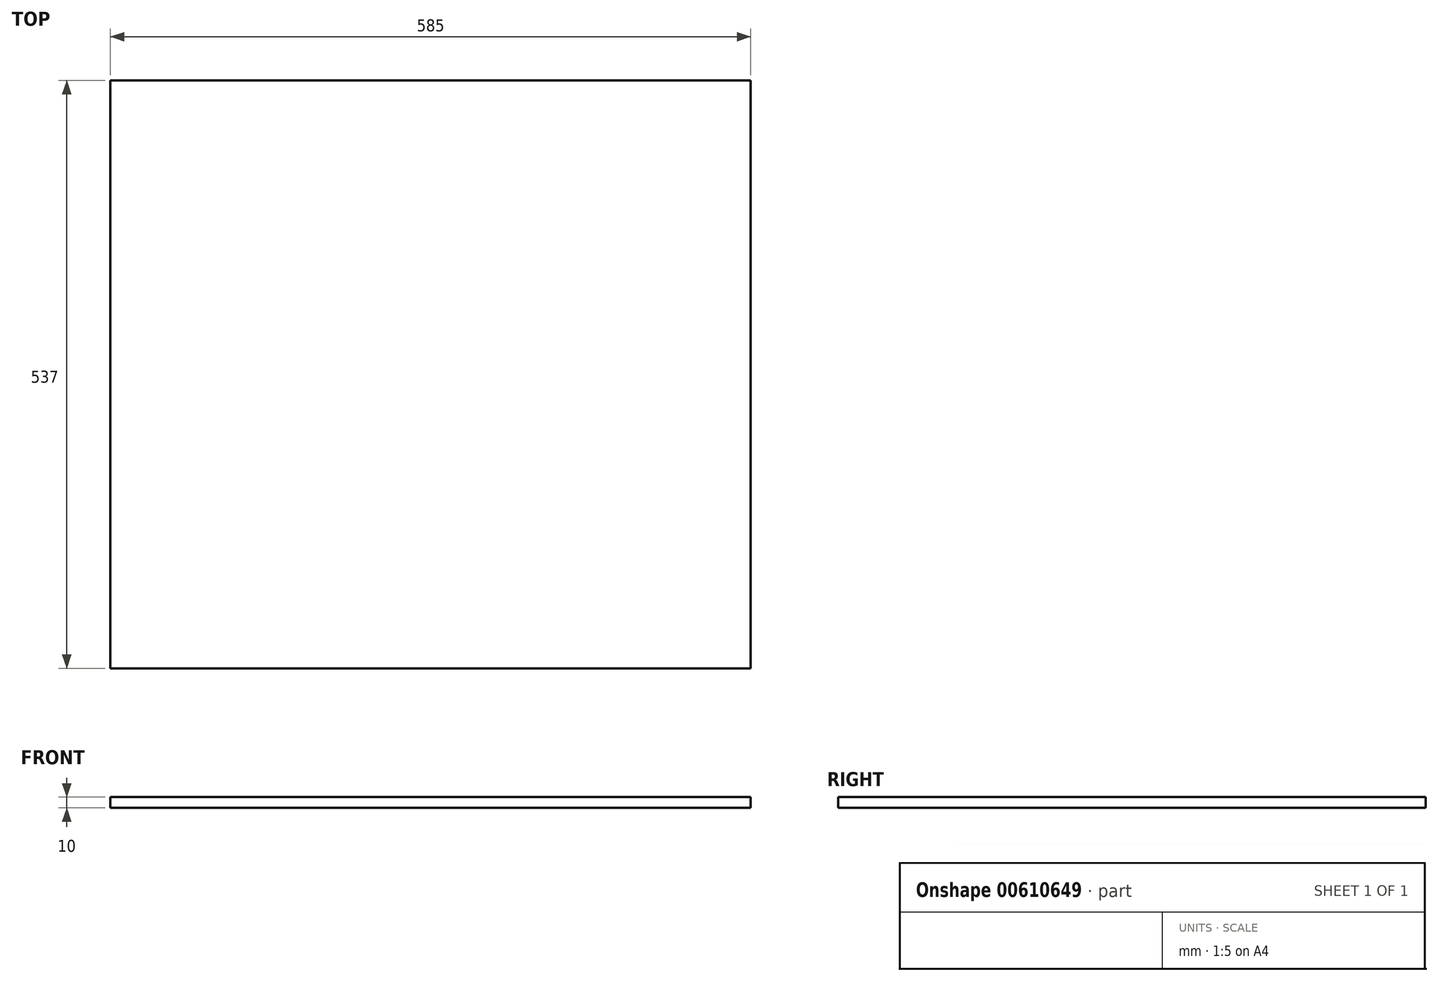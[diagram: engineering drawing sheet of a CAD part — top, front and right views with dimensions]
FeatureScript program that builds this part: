
annotation { "Feature Type Name" : "Feature", "Feature Type Description" : "" }
export const myFeature = defineFeature(function(context is Context, id is Id, definition is map)
    precondition{}
    {
        {
            var Q0;
            Q0=qCreatedBy(makeId("Top.planeOp"),FACE);
            var sketch = newSketch(context, id + "F0", { "sketchPlane" : qUnion([Q0])});
            skLineSegment(sketch, "E0.bottom", {"start": v(-336.36, 210.6) * mm, "end": v(248.64, 210.6) * mm});
            skLineSegment(sketch, "E0.top", {"start": v(-336.36, -326.4) * mm, "end": v(248.64, -326.4) * mm});
            skLineSegment(sketch, "E0.left", {"start": v(-336.36, 210.6) * mm, "end": v(-336.36, -326.4) * mm});
            skLineSegment(sketch, "E0.right", {"start": v(248.64, 210.6) * mm, "end": v(248.64, -326.4) * mm});
            skSolve(sketch);
        }
        {
            var Q0;
            Q0=makeQuery(id+"F0.imprint","IMPRINT",FACE,{"disambiguationData":[TD([[makeQuery(id+"F0.imprint","IMPRINT",EDGE,{"derivedFrom":sQuery(id+"F0.wireOp",EDGE,"E0.bottom")}),-1.0]])]});
            extrude(context, id + "F1", {"entities" : qUnion([Q0]), "depth" : 10 * mm, "offsetDistance" : 25 * mm});
        }
    });
